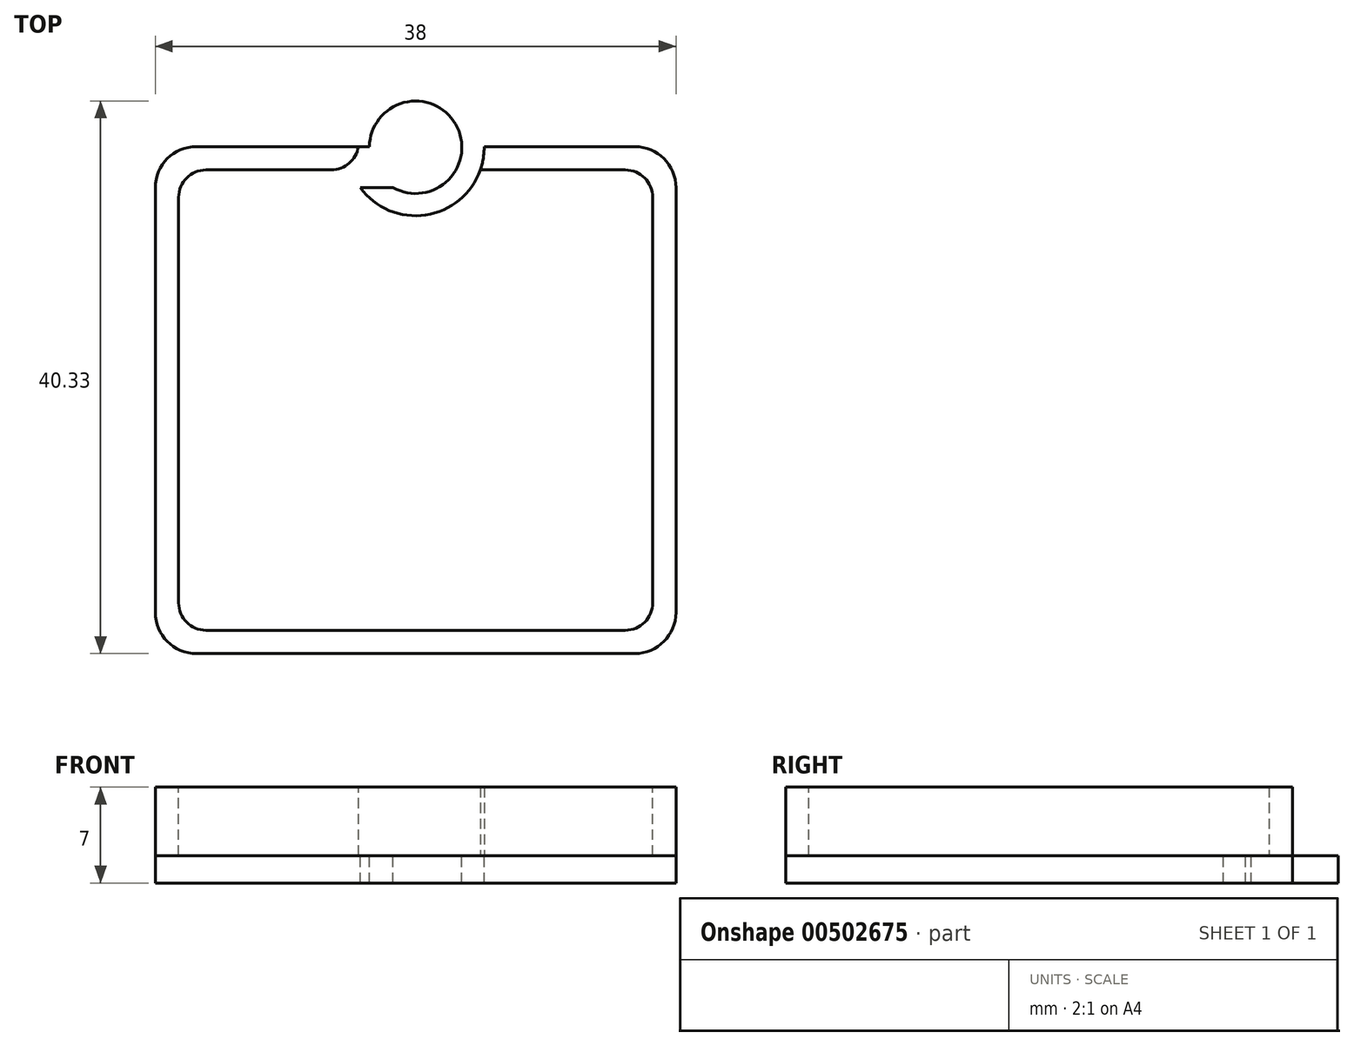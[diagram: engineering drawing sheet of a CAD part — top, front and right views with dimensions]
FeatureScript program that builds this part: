
annotation { "Feature Type Name" : "Feature", "Feature Type Description" : "" }
export const myFeature = defineFeature(function(context is Context, id is Id, definition is map)
    precondition{}
    {
        {
            var Q0;
            Q0=qCreatedBy(makeId("Top.planeOp"),FACE);
            var sketch = newSketch(context, id + "F0", { "sketchPlane" : qUnion([Q0])});
            skLineSegment(sketch, "E0.bottom", {"start": v(16, -15.5) * mm, "end": v(-16, -15.5) * mm});
            skLineSegment(sketch, "E0.top", {"start": v(16, 15.5) * mm, "end": v(-16, 15.5) * mm});
            skLineSegment(sketch, "E0.left", {"start": v(16, -15.5) * mm, "end": v(16, 15.5) * mm});
            skLineSegment(sketch, "E0.right", {"start": v(-16, -15.5) * mm, "end": v(-16, 15.5) * mm});
            skPoint(sketch, "E0.middle", {"position": v(0, 0) * mm});
            skLineSegment(sketch, "E1.bottom", {"start": v(19, -18.5) * mm, "end": v(-19, -18.5) * mm});
            skLineSegment(sketch, "E1.top", {"start": v(19, 18.5) * mm, "end": v(-19, 18.5) * mm});
            skLineSegment(sketch, "E1.left", {"start": v(19, -18.5) * mm, "end": v(19, 18.5) * mm});
            skLineSegment(sketch, "E1.right", {"start": v(-19, -18.5) * mm, "end": v(-19, 18.5) * mm});
            skCircle(sketch, "E2", {"center": v(0, 18.45) * mm, "radius": 3.38 * mm});
            skCircle(sketch, "E3", {"center": v(0, 18.45) * mm, "radius": 5 * mm});
            skSolve(sketch);
        }
        {
            var Q0;
            Q0=makeQuery(id+"F0.imprint","IMPRINT",FACE,{"disambiguationData":[TD([[makeQuery(id+"F0.imprint","IMPRINT",EDGE,{"derivedFrom":sQuery(id+"F0.wireOp",EDGE,"E0.bottom")}),-1.0]])]});
            var Q1;
            Q1=makeQuery(id+"F0.imprint","IMPRINT",FACE,{"disambiguationData":[TD([[makeQuery(id+"F0.imprint","IMPRINT",EDGE,{"derivedFrom":sQuery(id+"F0.wireOp",EDGE,"E0.bottom")}),1.0]])]});
            var Q2;
            {var subQ0=sQuery(id+"F0.wireOp",EDGE,"E2");var subQ1=sQuery(id+"F0.wireOp",EDGE,"E1.top");var subQ2=makeQuery(id+"F0.imprint","INTERSECT",VERTEX,{"disambiguationData":[OD(0.0)],"derivedFrom":[subQ1,subQ0]});Q2=makeQuery(id+"F0.imprint","IMPRINT",FACE,{"disambiguationData":[TD([[makeQuery(id+"F0.imprint","IMPRINT",EDGE,{"disambiguationData":[TD([[subQ2,-1.0]])],"derivedFrom":subQ1}),1.0]])]});}
            var Q3;
            {var subQ0=sQuery(id+"F0.wireOp",EDGE,"E2");var subQ1=sQuery(id+"F0.wireOp",EDGE,"E1.top");var subQ2=makeQuery(id+"F0.imprint","INTERSECT",VERTEX,{"disambiguationData":[OD(0.0)],"derivedFrom":[subQ1,subQ0]});Q3=makeQuery(id+"F0.imprint","IMPRINT",FACE,{"disambiguationData":[TD([[makeQuery(id+"F0.imprint","IMPRINT",EDGE,{"disambiguationData":[TD([[subQ2,-1.0]])],"derivedFrom":subQ1}),-1.0]])]});}
            var Q4;
            {var subQ0=sQuery(id+"F0.wireOp",EDGE,"E3");var subQ1=sQuery(id+"F0.wireOp",EDGE,"E1.top");var subQ2=makeQuery(id+"F0.imprint","INTERSECT",VERTEX,{"disambiguationData":[OD(0.0)],"derivedFrom":[subQ1,subQ0]});Q4=makeQuery(id+"F0.imprint","IMPRINT",FACE,{"disambiguationData":[TD([[makeQuery(id+"F0.imprint","IMPRINT",EDGE,{"disambiguationData":[TD([[subQ2,-1.0]])],"derivedFrom":subQ1}),-1.0]])]});}
            var Q5;
            {var subQ0=sQuery(id+"F0.wireOp",EDGE,"E3");var subQ1=sQuery(id+"F0.wireOp",EDGE,"E0.top");var subQ2=makeQuery(id+"F0.imprint","INTERSECT",VERTEX,{"disambiguationData":[OD(0.0)],"derivedFrom":[subQ1,subQ0]});Q5=makeQuery(id+"F0.imprint","IMPRINT",FACE,{"disambiguationData":[TD([[makeQuery(id+"F0.imprint","IMPRINT",EDGE,{"disambiguationData":[TD([[subQ2,-1.0]])],"derivedFrom":subQ1}),-1.0]])]});}
            var Q6;
            {var subQ0=sQuery(id+"F0.wireOp",EDGE,"E2");var subQ1=sQuery(id+"F0.wireOp",EDGE,"E0.top");var subQ2=makeQuery(id+"F0.imprint","INTERSECT",VERTEX,{"derivedFrom":[subQ1,subQ0]});Q6=makeQuery(id+"F0.imprint","IMPRINT",FACE,{"disambiguationData":[TD([[makeQuery(id+"F0.imprint","IMPRINT",EDGE,{"disambiguationData":[TD([[subQ2,-1.0]])],"derivedFrom":subQ1}),-1.0]])]});}
            var Q7;
            {var subQ0=sQuery(id+"F0.wireOp",EDGE,"E3");var subQ1=sQuery(id+"F0.wireOp",EDGE,"E0.top");var subQ2=makeQuery(id+"F0.imprint","INTERSECT",VERTEX,{"disambiguationData":[OD(0.0)],"derivedFrom":[subQ1,subQ0]});Q7=makeQuery(id+"F0.imprint","IMPRINT",FACE,{"disambiguationData":[TD([[makeQuery(id+"F0.imprint","IMPRINT",EDGE,{"disambiguationData":[TD([[subQ2,-1.0]])],"derivedFrom":subQ1}),1.0]])]});}
            var Q8;
            {var subQ0=sQuery(id+"F0.wireOp",EDGE,"E3");var subQ2=sQuery(id+"F0.wireOp",EDGE,"E1.top");var subQ7=makeQuery(id+"F0.imprint","INTERSECT",VERTEX,{"disambiguationData":[OD(0.0)],"derivedFrom":[subQ2,subQ0]});Q8=makeQuery(id+"F0.imprint","IMPRINT",FACE,{"disambiguationData":[TD([[makeQuery(id+"F0.imprint","IMPRINT",EDGE,{"disambiguationData":[TD([[subQ7,-1.0]])],"derivedFrom":subQ2}),1.0]])]});}
            var Q9;
            {var subQ0=sQuery(id+"F0.wireOp",EDGE,"E2");var subQ1=sQuery(id+"F0.wireOp",EDGE,"E0.top");var subQ2=makeQuery(id+"F0.imprint","INTERSECT",VERTEX,{"disambiguationData":[OD(0.0)],"derivedFrom":[subQ1,subQ0]});Q9=makeQuery(id+"F0.imprint","IMPRINT",FACE,{"disambiguationData":[TD([[makeQuery(id+"F0.imprint","IMPRINT",EDGE,{"disambiguationData":[TD([[subQ2,-1.0]])],"derivedFrom":subQ1}),1.0]])]});}
            extrude(context, id + "F1", {"entities" : qUnion([Q0, Q1, Q2, Q3, Q4, Q5, Q6, Q7, Q8, Q9]), "oppositeDirection" : true, "depth" : 2 * mm});
        }
        {
            var Q0;
            {var subQ0=sQuery(id+"F0.wireOp",EDGE,"E3");var subQ1=sQuery(id+"F0.wireOp",EDGE,"E1.top");var subQ2=makeQuery(id+"F0.imprint","INTERSECT",VERTEX,{"disambiguationData":[OD(0.0)],"derivedFrom":[subQ1,subQ0]});Q0=makeQuery(id+"F0.imprint","IMPRINT",FACE,{"disambiguationData":[TD([[makeQuery(id+"F0.imprint","IMPRINT",EDGE,{"disambiguationData":[TD([[subQ2,-1.0]])],"derivedFrom":subQ1}),-1.0]])]});}
            var Q1;
            Q1=makeQuery(id+"F0.imprint","IMPRINT",FACE,{"disambiguationData":[TD([[makeQuery(id+"F0.imprint","IMPRINT",EDGE,{"derivedFrom":sQuery(id+"F0.wireOp",EDGE,"E0.bottom")}),1.0]])]});
            var Q2;
            {var subQ0=sQuery(id+"F0.wireOp",EDGE,"E3");var subQ2=sQuery(id+"F0.wireOp",EDGE,"E1.top");var subQ7=makeQuery(id+"F0.imprint","INTERSECT",VERTEX,{"disambiguationData":[OD(0.0)],"derivedFrom":[subQ2,subQ0]});Q2=makeQuery(id+"F0.imprint","IMPRINT",FACE,{"disambiguationData":[TD([[makeQuery(id+"F0.imprint","IMPRINT",EDGE,{"disambiguationData":[TD([[subQ7,-1.0]])],"derivedFrom":subQ2}),1.0]])]});}
            var Q3;
            {var subQ0=sQuery(id+"F0.wireOp",EDGE,"E2");var subQ1=sQuery(id+"F0.wireOp",EDGE,"E0.top");var subQ2=makeQuery(id+"F0.imprint","INTERSECT",VERTEX,{"disambiguationData":[OD(1.0)],"derivedFrom":[subQ1,subQ0]});Q3=makeQuery(id+"F0.imprint","IMPRINT",FACE,{"disambiguationData":[TD([[makeQuery(id+"F0.imprint","IMPRINT",EDGE,{"disambiguationData":[TD([[subQ2,-1.0]])],"derivedFrom":subQ1}),-1.0]])]});}
            extrude(context, id + "F2", {"entities" : qUnion([Q0, Q1, Q2, Q3]), "depth" : 5 * mm});
        }
        {
            var Q0;
            Q0=makeQuery(id+"F2.opExtrude","CAP_FACE",FACE,{"disambiguationData":[OSD([sQuery(id+"F0.wireOp",EDGE,"E0.bottom"),sQuery(id+"F0.wireOp",EDGE,"E0.top"),sQuery(id+"F0.wireOp",EDGE,"E0.left"),sQuery(id+"F0.wireOp",EDGE,"E0.right"),sQuery(id+"F0.wireOp",EDGE,"E1.bottom"),sQuery(id+"F0.wireOp",EDGE,"E1.top"),sQuery(id+"F0.wireOp",EDGE,"E1.left"),sQuery(id+"F0.wireOp",EDGE,"E1.right"),sQuery(id+"F0.wireOp",EDGE,"E2"),sQuery(id+"F0.wireOp",EDGE,"E3")])],"isStart":false});
            var sketch = newSketch(context, id + "F3", { "sketchPlane" : qUnion([Q0])});
            skLineSegment(sketch, "E4.bottom", {"start": v(17.3, -16.8) * mm, "end": v(-17.3, -16.8) * mm});
            skLineSegment(sketch, "E4.top", {"start": v(17.3, 16.8) * mm, "end": v(-17.3, 16.8) * mm});
            skLineSegment(sketch, "E4.left", {"start": v(17.3, -16.8) * mm, "end": v(17.3, 16.8) * mm});
            skLineSegment(sketch, "E4.right", {"start": v(-17.3, -16.8) * mm, "end": v(-17.3, 16.8) * mm});
            skPoint(sketch, "E4.middle", {"position": v(0, 0) * mm});
            skCircle(sketch, "E5", {"center": v(0, 18.45) * mm, "radius": 4.17 * mm});
            skSolve(sketch);
        }
        {
            var Q0;
            Q0=makeQuery(id+"F2.opExtrude","SWEPT_EDGE",EDGE,{"disambiguationData":[OSD([sQuery(id+"F0.wireOp",EDGE,"E1.top"),sQuery(id+"F0.wireOp",EDGE,"E1.left")])]});
            var Q1;
            Q1=makeQuery(id+"F2.opExtrude","SWEPT_EDGE",EDGE,{"disambiguationData":[OSD([sQuery(id+"F0.wireOp",EDGE,"E1.top"),sQuery(id+"F0.wireOp",EDGE,"E1.right")])]});
            var Q2;
            Q2=makeQuery(id+"F2.opExtrude","SWEPT_EDGE",EDGE,{"disambiguationData":[OSD([sQuery(id+"F0.wireOp",EDGE,"E1.bottom"),sQuery(id+"F0.wireOp",EDGE,"E1.left")])]});
            var Q3;
            Q3=makeQuery(id+"F2.opExtrude","SWEPT_EDGE",EDGE,{"disambiguationData":[OSD([sQuery(id+"F0.wireOp",EDGE,"E1.bottom"),sQuery(id+"F0.wireOp",EDGE,"E1.right")])]});
            var Q4;
            Q4=makeQuery(id+"F1.opExtrude","SWEPT_EDGE",EDGE,{"disambiguationData":[OSD([sQuery(id+"F0.wireOp",EDGE,"E1.bottom"),sQuery(id+"F0.wireOp",EDGE,"E1.right")])]});
            var Q5;
            Q5=makeQuery(id+"F1.opExtrude","SWEPT_EDGE",EDGE,{"disambiguationData":[OSD([sQuery(id+"F0.wireOp",EDGE,"E1.bottom"),sQuery(id+"F0.wireOp",EDGE,"E1.left")])]});
            var Q6;
            Q6=makeQuery(id+"F1.opExtrude","SWEPT_EDGE",EDGE,{"disambiguationData":[OSD([sQuery(id+"F0.wireOp",EDGE,"E1.top"),sQuery(id+"F0.wireOp",EDGE,"E1.left")])]});
            var Q7;
            Q7=makeQuery(id+"F1.opExtrude","SWEPT_EDGE",EDGE,{"disambiguationData":[OSD([sQuery(id+"F0.wireOp",EDGE,"E1.top"),sQuery(id+"F0.wireOp",EDGE,"E1.right")])]});
            fillet(context, id + "F4", {"entities" : qUnion([Q0, Q1, Q2, Q3, Q4, Q5, Q6, Q7]), "radius" : 3 * mm, "tangentPropagation" : true, "allowEdgeOverflow" : false});
        }
        {
            var Q0;
            Q0 = qSketchRegion(id + "F3", true);
            extrude(context, id + "F5", {"entities" : qUnion([Q0]), "operationType" : NewBodyOperationType.REMOVE, "oppositeDirection" : true, "depth" : 5 * mm});
        }
        {
            var Q0;
            Q0=makeQuery(id+"F5.boolean.opBoolean","COPY",EDGE,{"derivedFrom":makeQuery(id+"F5.opExtrude","SWEPT_EDGE",EDGE,{"disambiguationData":[OSD([sQuery(id+"F3.wireOp",EDGE,"E4.top"),sQuery(id+"F3.wireOp",EDGE,"E4.right")])]})});
            var Q1;
            Q1=makeQuery(id+"F5.boolean.opBoolean","COPY",EDGE,{"derivedFrom":makeQuery(id+"F5.opExtrude","SWEPT_EDGE",EDGE,{"disambiguationData":[OSD([sQuery(id+"F3.wireOp",EDGE,"E4.top"),sQuery(id+"F3.wireOp",EDGE,"E4.left")])]})});
            var Q2;
            Q2=makeQuery(id+"F5.boolean.opBoolean","COPY",EDGE,{"derivedFrom":makeQuery(id+"F5.opExtrude","SWEPT_EDGE",EDGE,{"disambiguationData":[OSD([sQuery(id+"F3.wireOp",EDGE,"E4.bottom"),sQuery(id+"F3.wireOp",EDGE,"E4.left")])]})});
            var Q3;
            Q3=makeQuery(id+"F5.boolean.opBoolean","COPY",EDGE,{"derivedFrom":makeQuery(id+"F5.opExtrude","SWEPT_EDGE",EDGE,{"disambiguationData":[OSD([sQuery(id+"F3.wireOp",EDGE,"E4.bottom"),sQuery(id+"F3.wireOp",EDGE,"E4.right")])]})});
            fillet(context, id + "F6", {"entities" : qUnion([Q0, Q1, Q2, Q3]), "radius" : 2 * mm, "tangentPropagation" : true, "allowEdgeOverflow" : false});
        }
        {
            var Q0;
            {var subQ0=sQuery(id+"F3.wireOp",EDGE,"E5");var subQ1=sQuery(id+"F3.wireOp",EDGE,"E4.top");Q0=makeQuery(id+"F5.boolean.opBoolean","COPY",EDGE,{"derivedFrom":makeQuery(id+"F5.opExtrude","SWEPT_EDGE",EDGE,{"disambiguationData":[OSD([subQ1,subQ0]),TDD([makeQuery(id+"F3.imprint","INTERSECT",VERTEX,{"disambiguationData":[OD(1.0)],"derivedFrom":[subQ1,subQ0]})])]})});}
            var Q1;
            {var subQ0=sQuery(id+"F3.wireOp",EDGE,"E5");var subQ1=sQuery(id+"F3.wireOp",EDGE,"E4.top");Q1=makeQuery(id+"F5.boolean.opBoolean","COPY",EDGE,{"derivedFrom":makeQuery(id+"F5.opExtrude","SWEPT_EDGE",EDGE,{"disambiguationData":[OSD([subQ1,subQ0]),TDD([makeQuery(id+"F3.imprint","INTERSECT",VERTEX,{"disambiguationData":[OD(0.0)],"derivedFrom":[subQ1,subQ0]})])]})});}
            fillet(context, id + "F7", {"entities" : qUnion([Q0, Q1]), "radius" : 2 * mm, "tangentPropagation" : true, "allowEdgeOverflow" : false});
        }
    });
